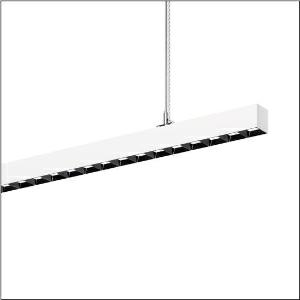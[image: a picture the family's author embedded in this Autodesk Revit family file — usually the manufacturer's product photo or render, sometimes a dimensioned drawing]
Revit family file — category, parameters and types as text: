
# Revit family: silica_r__21_51mx34dc4dwb_1888
name_source: partatom
category: Lighting Fixtures
units: mm (PartAtom-declared; Revit-internal decimal feet)

## family parameters
Cut with Voids When Loaded = No
Host = Face
Light Source = No
Part Type = Normal
Room Calculation Point = No
Round Connector Dimension = Use Diameter
Shared = No

## types (1)
- --- (1 x LED, 19200 lm, 120.3 W, 4000K)
    Apparent Load = 120 VA
    CIE Flux Codes = 74 94 99 56 100
    Color Rendering = 80
    Color Temperature = 4000K
    Default Elevation = 1800 mm
    Description = Silica® 21, office luminaire, primary light control with darklight reflector, of PMMA, black, light emission: direct/indirect distribution, primary light characteristic: asymmetric, installation type: suspended mounting, LED, rated luminous flux: 19.200lm, luminous efficacy: 160lm/W, light colour: 840, colour temperature: 4000K, with terminal, 3+2-pole, max. 2.5mm², mains connection: 220..240V, AC, 50/60Hz, rated input power: 120.3W, luminaire housing, of aluminium, traffic white (RAL 9016), length: 3.004mm, width: 53mm, height: 53mm, protection rating (complete): IP20, insulation class (complete): insulation class I (protective earthing), certification: CE, permissible operating ambient temperature: 0..+35°C, standard: EN 50419, packaging unit: 1 piece
    Height = 53 mm
    Lamp = 1 x LED
    Lamp Light Flux = 19200 lm
    Lamp Power = 120.3 W
    Lamp count = 1
    Length = 3004 mm
    Luminous efficacy = 160 lm/W
    Manufacturer = Siteco
    ModVariant = No
    Model = 51MX34DC4DWB
    Mounting Place = Ceiling
    Mounting Type = Pendant
    Number of Poles = 1
    OnlyDefault = Yes
    Power Factor = 1
    Product Name = Silica® 21
    Product group = office luminaire | ceiling pendant
    ProductGroupID = 902
    Protection Class = Protection class I
    Protection Degree = IP 20
    RLX_Detail_Level = 1
    RLX_Emergency_Light_Flux = 0 lm
    RLX_Emergency_Type = 0
    RLX_Emergency_Type_DB = No
    RlxData = <blob elided: 65445 chars, md5=6a2ff757>
    Socket = socket
    Standby Power = 0 W
    System Light Flux = 19200 lm
    System Power = 120 W
    Type Comments = factory setting: luminous flux: 100 % | dim-lin: 254 | 418 mA
    Type Image = l_1335871.jpg
    URL = http://relux.com
    VarID = @adj_089807
    Voltage = 0 V
    Weight = 0.00 kg
    Width = 53 mm

## geometry (parser evidence)
native form markers: Blend x4, Sweep x15
no freeform markers — native parametric forms only
